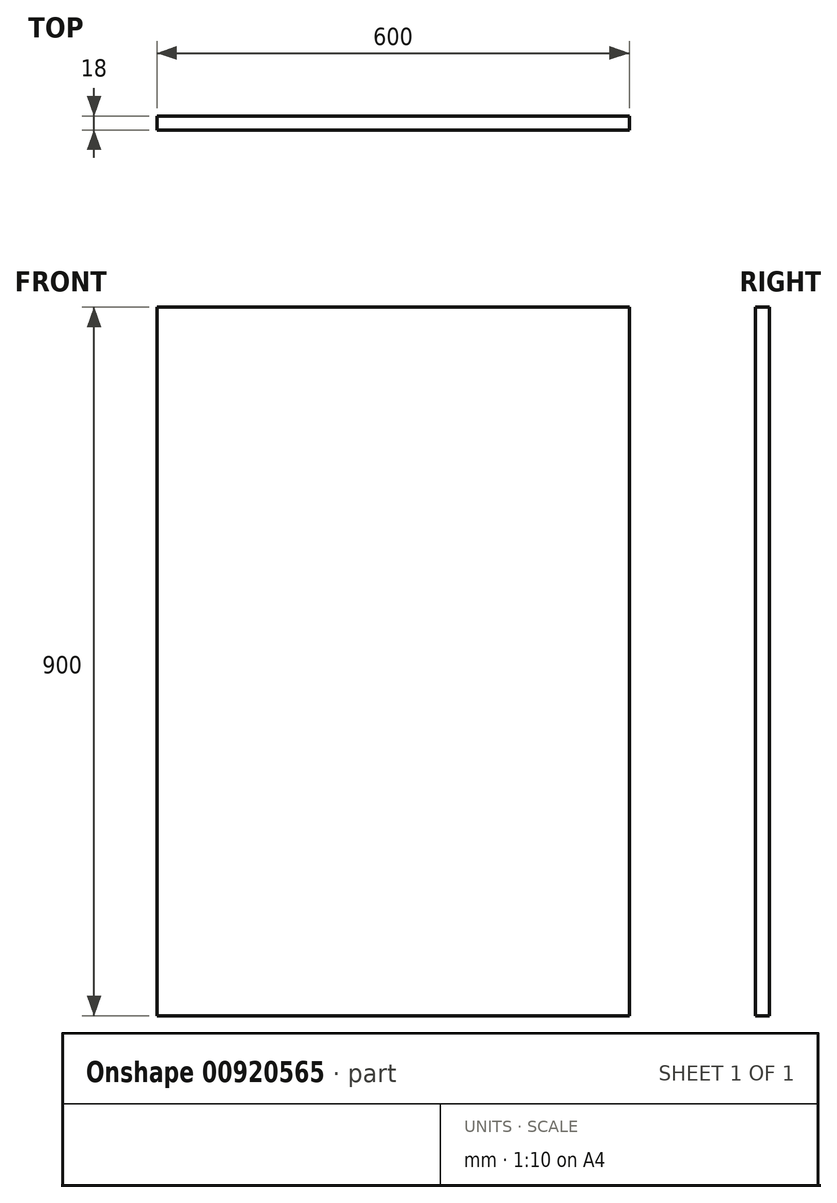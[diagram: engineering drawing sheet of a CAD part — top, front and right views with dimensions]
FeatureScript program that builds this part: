
annotation { "Feature Type Name" : "Feature", "Feature Type Description" : "" }
export const myFeature = defineFeature(function(context is Context, id is Id, definition is map)
    precondition{}
    {
        {
            var Q0;
            Q0=qCreatedBy(makeId("Front.planeOp"),FACE);
            var sketch = newSketch(context, id + "F0", { "sketchPlane" : qUnion([Q0])});
            skLineSegment(sketch, "E0.bottom", {"start": v(300, -450) * mm, "end": v(-300, -450) * mm});
            skLineSegment(sketch, "E0.top", {"start": v(300, 450) * mm, "end": v(-300, 450) * mm});
            skLineSegment(sketch, "E0.left", {"start": v(300, -450) * mm, "end": v(300, 450) * mm});
            skLineSegment(sketch, "E0.right", {"start": v(-300, -450) * mm, "end": v(-300, 450) * mm});
            skPoint(sketch, "E0.middle", {"position": v(0, 0) * mm});
            skSolve(sketch);
        }
        {
            var Q0;
            Q0=qSketchRegion(id+"F0",true);
            extrude(context, id + "F1", {"entities" : qUnion([Q0]), "depth" : 18 * mm, "offsetDistance" : 25 * mm, "symmetric" : true});
        }
    });
